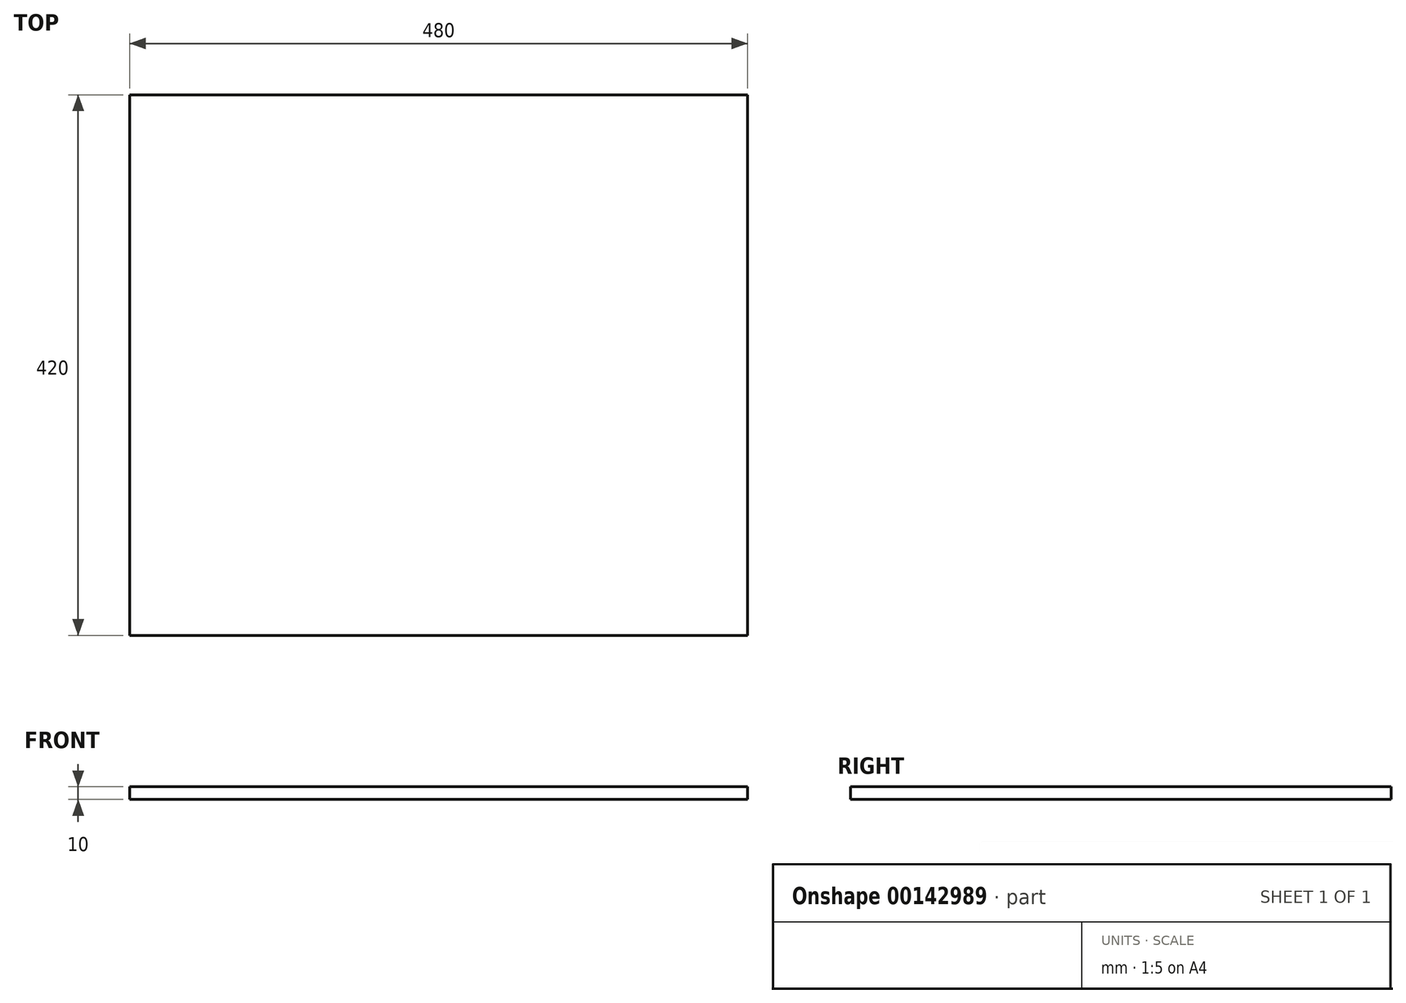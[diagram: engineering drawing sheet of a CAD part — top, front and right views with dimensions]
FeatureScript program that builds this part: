
annotation { "Feature Type Name" : "Feature", "Feature Type Description" : "" }
export const myFeature = defineFeature(function(context is Context, id is Id, definition is map)
    precondition{}
    {
        {
            var Q0;
            Q0=qCreatedBy(makeId("Top.planeOp"),FACE);
            var sketch = newSketch(context, id + "F0", { "sketchPlane" : qUnion([Q0])});
            skLineSegment(sketch, "E0.bottom", {"start": v(0, 0) * mm, "end": v(480, 0) * mm});
            skLineSegment(sketch, "E0.top", {"start": v(0, 420) * mm, "end": v(480, 420) * mm});
            skLineSegment(sketch, "E0.left", {"start": v(0, 0) * mm, "end": v(0, 420) * mm});
            skLineSegment(sketch, "E0.right", {"start": v(480, 0) * mm, "end": v(480, 420) * mm});
            skSolve(sketch);
        }
        {
            var Q0;
            Q0 = qSketchRegion(id + "F0", true);
            extrude(context, id + "F1", {"entities" : qUnion([Q0]), "depth" : 10 * mm, "offsetDistance" : 25 * mm});
        }
    });
